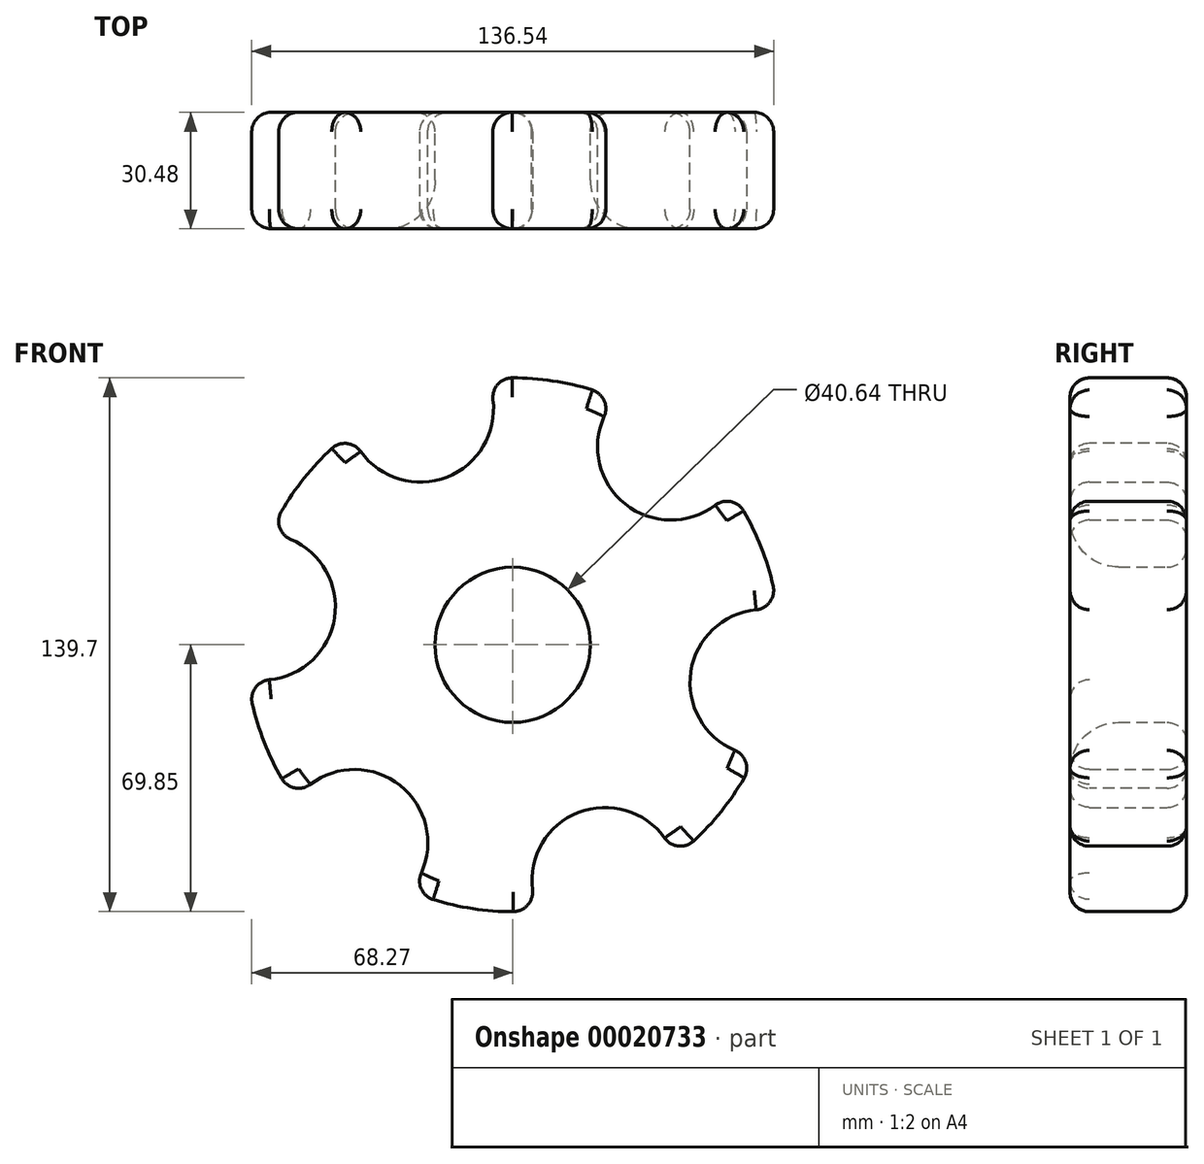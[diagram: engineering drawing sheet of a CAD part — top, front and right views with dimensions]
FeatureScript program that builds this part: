
annotation { "Feature Type Name" : "Feature", "Feature Type Description" : "" }
export const myFeature = defineFeature(function(context is Context, id is Id, definition is map)
    precondition{}
    {
        {
            var Q0;
            Q0=qCreatedBy(makeId("Front.planeOp"),FACE);
            var sketch = newSketch(context, id + "F0", { "sketchPlane" : qUnion([Q0])});
            skCircle(sketch, "E0", {"center": v(0, 0) * mm, "radius": 69.85 * mm});
            skSolve(sketch);
        }
        {
            var Q0;
            Q0 = qSketchRegion(id + "F0", true);
            extrude(context, id + "F1", {"entities" : qUnion([Q0]), "depth" : 30.48 * mm});
        }
        {
            var Q0;
            Q0=makeQuery(id+"F1.opExtrude","CAP_FACE",FACE,{"disambiguationData":[OSD([sQuery(id+"F0.wireOp",EDGE,"E0")])],"isStart":true});
            var sketch = newSketch(context, id + "F2", { "sketchPlane" : qUnion([Q0])});
            skCircle(sketch, "E1", {"center": v(0, 0) * mm, "radius": 20.32 * mm});
            skArc(sketch, "E2", {"start": v(-42.33, -55.56) * mm, "mid": v(-25.47, -65.04) * mm, "end": v(-6.65, -69.53) * mm});
            skArc(sketch, "E3", {"start": v(-6.65, -69.53) * mm, "mid": v(-17.19, -43.9) * mm, "end": v(-42.33, -55.56) * mm});
            skArc(sketch, "E4.1.0", {"start": v(26.95, -64.44) * mm, "mid": v(43.6, -54.58) * mm, "end": v(56.9, -40.53) * mm});
            skArc(sketch, "E4.1.1", {"start": v(56.9, -40.53) * mm, "mid": v(29.42, -36.83) * mm, "end": v(26.95, -64.44) * mm});
            skArc(sketch, "E4.2.0", {"start": v(69.28, -8.88) * mm, "mid": v(69.06, 10.46) * mm, "end": v(63.54, 29) * mm});
            skArc(sketch, "E4.2.1", {"start": v(63.54, 29) * mm, "mid": v(46.6, 7.06) * mm, "end": v(69.28, -8.88) * mm});
            skArc(sketch, "E4.3.0", {"start": v(42.33, 55.56) * mm, "mid": v(25.47, 65.04) * mm, "end": v(6.65, 69.53) * mm});
            skArc(sketch, "E4.3.1", {"start": v(6.65, 69.53) * mm, "mid": v(17.19, 43.9) * mm, "end": v(42.33, 55.56) * mm});
            skArc(sketch, "E4.4.0", {"start": v(-26.95, 64.44) * mm, "mid": v(-43.6, 54.58) * mm, "end": v(-56.9, 40.53) * mm});
            skArc(sketch, "E4.4.1", {"start": v(-56.9, 40.53) * mm, "mid": v(-29.42, 36.83) * mm, "end": v(-26.95, 64.44) * mm});
            skArc(sketch, "E4.5.0", {"start": v(-69.28, 8.88) * mm, "mid": v(-69.06, -10.46) * mm, "end": v(-63.54, -29) * mm});
            skArc(sketch, "E4.5.1", {"start": v(-63.54, -29) * mm, "mid": v(-46.6, -7.06) * mm, "end": v(-69.28, 8.88) * mm});
            skSolve(sketch);
        }
        {
            var Q0;
            Q0=makeQuery(id+"F2.imprint","IMPRINT",FACE,{"disambiguationData":[TD([[makeQuery(id+"F2.imprint","IMPRINT",EDGE,{"derivedFrom":sQuery(id+"F2.wireOp",EDGE,"E1")}),1.0]])]});
            var Q1;
            Q1=makeQuery(id+"F2.imprint","IMPRINT",FACE,{"disambiguationData":[TD([[makeQuery(id+"F2.imprint","IMPRINT",EDGE,{"derivedFrom":sQuery(id+"F2.wireOp",EDGE,"E4.1.0")}),-1.0]])]});
            var Q2;
            Q2=makeQuery(id+"F2.imprint","IMPRINT",FACE,{"disambiguationData":[TD([[makeQuery(id+"F2.imprint","IMPRINT",EDGE,{"derivedFrom":sQuery(id+"F2.wireOp",EDGE,"E2")}),-1.0]])]});
            var Q3;
            Q3=makeQuery(id+"F2.imprint","IMPRINT",FACE,{"disambiguationData":[TD([[makeQuery(id+"F2.imprint","IMPRINT",EDGE,{"derivedFrom":sQuery(id+"F2.wireOp",EDGE,"E4.5.0")}),-1.0]])]});
            var Q4;
            Q4=makeQuery(id+"F2.imprint","IMPRINT",FACE,{"disambiguationData":[TD([[makeQuery(id+"F2.imprint","IMPRINT",EDGE,{"derivedFrom":sQuery(id+"F2.wireOp",EDGE,"E4.4.0")}),-1.0]])]});
            var Q5;
            Q5=makeQuery(id+"F2.imprint","IMPRINT",FACE,{"disambiguationData":[TD([[makeQuery(id+"F2.imprint","IMPRINT",EDGE,{"derivedFrom":sQuery(id+"F2.wireOp",EDGE,"E4.3.0")}),-1.0]])]});
            var Q6;
            Q6=makeQuery(id+"F2.imprint","IMPRINT",FACE,{"disambiguationData":[TD([[makeQuery(id+"F2.imprint","IMPRINT",EDGE,{"derivedFrom":sQuery(id+"F2.wireOp",EDGE,"E4.2.0")}),-1.0]])]});
            extrude(context, id + "F3", {"entities" : qUnion([Q0, Q1, Q2, Q3, Q4, Q5, Q6]), "operationType" : NewBodyOperationType.REMOVE, "endBound" : BoundingType.THROUGH_ALL, "oppositeDirection" : true, "depth" : 25.4 * mm});
        }
        {
            var Q0;
            Q0=makeQuery(id+"F3.boolean.opBoolean","INTERSECT",EDGE,{"derivedFrom":[makeQuery(id+"F1.opExtrude","CAP_FACE",FACE,{"disambiguationData":[OSD([sQuery(id+"F0.wireOp",EDGE,"E0")])],"isStart":false}),makeQuery(id+"F3.opExtrude","SWEPT_FACE",FACE,{"disambiguationData":[OSD([sQuery(id+"F2.wireOp",EDGE,"E1")])]})]});
            var Q1;
            Q1=makeQuery(id+"F3.boolean.opBoolean","COPY",EDGE,{"derivedFrom":makeQuery(id+"F3.opExtrude","CAP_EDGE",EDGE,{"disambiguationData":[OSD([sQuery(id+"F2.wireOp",EDGE,"E1")])],"isStart":true})});
            fillet(context, id + "F4", {"entities" : qUnion([Q0, Q1]), "radius" : 12.7 * mm, "allowEdgeOverflow" : false});
        }
        {
            var Q0;
            Q0=makeQuery(id+"F3.boolean.opBoolean","COPY",EDGE,{"derivedFrom":makeQuery(id+"F3.opExtrude","CAP_EDGE",EDGE,{"disambiguationData":[OSD([sQuery(id+"F2.wireOp",EDGE,"E4.1.1")])],"isStart":true})});
            var Q1;
            {var subQ0=sQuery(id+"F0.wireOp",EDGE,"E0");var subQ1=sQuery(id+"F2.wireOp",EDGE,"E4.1.0");var subQ2=sQuery(id+"F2.wireOp",EDGE,"E4.1.1");Q1=makeQuery(id+"F3.boolean.opBoolean","COPY",EDGE,{"derivedFrom":makeQuery(id+"F3.opExtrude","SWEPT_EDGE",EDGE,{"disambiguationData":[OSD([subQ0,subQ1,subQ2]),TDD([makeQuery(id+"F2.imprint","INTERSECT",VERTEX,{"disambiguationData":[OD(0.0)],"derivedFrom":[makeQuery(id+"F1.opExtrude","CAP_EDGE",EDGE,{"disambiguationData":[OSD([subQ0])],"isStart":true}),subQ1,subQ2]})])]})});}
            var Q2;
            Q2=makeQuery(id+"F3.boolean.opBoolean","INTERSECT",EDGE,{"derivedFrom":[makeQuery(id+"F1.opExtrude","CAP_FACE",FACE,{"disambiguationData":[OSD([sQuery(id+"F0.wireOp",EDGE,"E0")])],"isStart":false}),makeQuery(id+"F3.opExtrude","SWEPT_FACE",FACE,{"disambiguationData":[OSD([sQuery(id+"F2.wireOp",EDGE,"E4.1.1")])]})]});
            var Q3;
            {var subQ0=sQuery(id+"F0.wireOp",EDGE,"E0");var subQ1=sQuery(id+"F2.wireOp",EDGE,"E4.1.0");var subQ2=sQuery(id+"F2.wireOp",EDGE,"E4.1.1");Q3=makeQuery(id+"F3.boolean.opBoolean","COPY",EDGE,{"derivedFrom":makeQuery(id+"F3.opExtrude","SWEPT_EDGE",EDGE,{"disambiguationData":[OSD([subQ0,subQ1,subQ2]),TDD([makeQuery(id+"F2.imprint","INTERSECT",VERTEX,{"disambiguationData":[OD(1.0)],"derivedFrom":[makeQuery(id+"F1.opExtrude","CAP_EDGE",EDGE,{"disambiguationData":[OSD([subQ0])],"isStart":true}),subQ1,subQ2]})])]})});}
            var Q4;
            {var subQ0=sQuery(id+"F0.wireOp",EDGE,"E0");var subQ1=sQuery(id+"F2.wireOp",EDGE,"E4.2.0");var subQ2=sQuery(id+"F2.wireOp",EDGE,"E4.2.1");Q4=makeQuery(id+"F3.boolean.opBoolean","COPY",EDGE,{"derivedFrom":makeQuery(id+"F3.opExtrude","SWEPT_EDGE",EDGE,{"disambiguationData":[OSD([subQ0,subQ1,subQ2]),TDD([makeQuery(id+"F2.imprint","INTERSECT",VERTEX,{"disambiguationData":[OD(1.0)],"derivedFrom":[makeQuery(id+"F1.opExtrude","CAP_EDGE",EDGE,{"disambiguationData":[OSD([subQ0])],"isStart":true}),subQ1,subQ2]})])]})});}
            var Q5;
            {var subQ0=sQuery(id+"F0.wireOp",EDGE,"E0");var subQ1=sQuery(id+"F2.wireOp",EDGE,"E4.2.0");var subQ2=sQuery(id+"F2.wireOp",EDGE,"E4.2.1");Q5=makeQuery(id+"F3.boolean.opBoolean","COPY",EDGE,{"derivedFrom":makeQuery(id+"F3.opExtrude","SWEPT_EDGE",EDGE,{"disambiguationData":[OSD([subQ0,subQ1,subQ2]),TDD([makeQuery(id+"F2.imprint","INTERSECT",VERTEX,{"disambiguationData":[OD(0.0)],"derivedFrom":[makeQuery(id+"F1.opExtrude","CAP_EDGE",EDGE,{"disambiguationData":[OSD([subQ0])],"isStart":true}),subQ1,subQ2]})])]})});}
            var Q6;
            Q6=makeQuery(id+"F3.boolean.opBoolean","INTERSECT",EDGE,{"derivedFrom":[makeQuery(id+"F1.opExtrude","CAP_FACE",FACE,{"disambiguationData":[OSD([sQuery(id+"F0.wireOp",EDGE,"E0")])],"isStart":false}),makeQuery(id+"F3.opExtrude","SWEPT_FACE",FACE,{"disambiguationData":[OSD([sQuery(id+"F2.wireOp",EDGE,"E4.2.1")])]})]});
            var Q7;
            Q7=makeQuery(id+"F3.boolean.opBoolean","COPY",EDGE,{"derivedFrom":makeQuery(id+"F3.opExtrude","CAP_EDGE",EDGE,{"disambiguationData":[OSD([sQuery(id+"F2.wireOp",EDGE,"E4.2.1")])],"isStart":true})});
            var Q8;
            Q8=makeQuery(id+"F3.boolean.opBoolean","COPY",FACE,{"derivedFrom":makeQuery(id+"F3.opExtrude","SWEPT_FACE",FACE,{"disambiguationData":[OSD([sQuery(id+"F2.wireOp",EDGE,"E3")])]})});
            var Q9;
            Q9=makeQuery(id+"F3.boolean.opBoolean","COPY",FACE,{"derivedFrom":makeQuery(id+"F3.opExtrude","SWEPT_FACE",FACE,{"disambiguationData":[OSD([sQuery(id+"F2.wireOp",EDGE,"E4.5.1")])]})});
            var Q10;
            Q10=makeQuery(id+"F3.boolean.opBoolean","COPY",FACE,{"derivedFrom":makeQuery(id+"F3.opExtrude","SWEPT_FACE",FACE,{"disambiguationData":[OSD([sQuery(id+"F2.wireOp",EDGE,"E4.4.1")])]})});
            var Q11;
            Q11=makeQuery(id+"F3.boolean.opBoolean","COPY",FACE,{"derivedFrom":makeQuery(id+"F3.opExtrude","SWEPT_FACE",FACE,{"disambiguationData":[OSD([sQuery(id+"F2.wireOp",EDGE,"E4.3.1")])]})});
            fillet(context, id + "F5", {"entities" : qUnion([Q0, Q1, Q2, Q3, Q4, Q5, Q6, Q7, Q8, Q9, Q10, Q11]), "radius" : 5.08 * mm, "tangentPropagation" : true, "allowEdgeOverflow" : false});
        }
        {
            var Q0;
            Q0=makeQuery(id+"F1.opExtrude","CAP_FACE",FACE,{"disambiguationData":[OSD([sQuery(id+"F0.wireOp",EDGE,"E0")])],"isStart":false});
            var Q1;
            Q1=makeQuery(id+"F1.opExtrude","CAP_FACE",FACE,{"disambiguationData":[OSD([sQuery(id+"F0.wireOp",EDGE,"E0")])],"isStart":true});
            fillet(context, id + "F6", {"entities" : qUnion([Q0, Q1]), "radius" : 5.08 * mm, "tangentPropagation" : true, "allowEdgeOverflow" : false});
        }
    });
